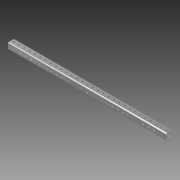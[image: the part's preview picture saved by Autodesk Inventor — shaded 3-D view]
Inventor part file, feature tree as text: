
AUTODESK INVENTOR PART (.ipt)
format: ipt  version: 2014 (Build 180170000, 170)  size: 184,320 bytes
history: native  units: in
note: dims shown in document units (in); Inventor stores cm internally (conversion verified against a paired STEP export)
features: sketch x3, extrude x2, chamfer x1, hole x1, pattern_linear x1
ambient origin geometry x8: Origin, YZ Plane, XZ Plane, XY Plane, X Axis, Y Axis, Z Axis, Center Point
bodies: Solid1 (feature_tree)
feature tree (8):
  extrude  "Extrusion1"  Depth=0.125in TaperAngle=45.0deg
  chamfer  "Chamfer1"  Distance=1.0in
  hole  "Hole1"  [1 undecoded]
  pattern_linear  "Rectangular Pattern1"  [2 undecoded]
  extrude  "Extrusion2"  [1 undecoded]
  sketch  "Sketch1"  dims[d0=30.0in d1=0.0in d2=0.125in d3=0.125in d4=45.0deg]
  sketch  "Sketch2"  dims[d5=0.5in]
  sketch  "Sketch3"  dims[d6=0.5in d7=0.264in d8=0.75in d9=0.375in d10=0.25in d11=0.5635in d12=1.0in d13=0.8108in d14=11.811in d16=1.0in d17=1.0in d18=0.0in]
note: 4 required parameter values undecoded (feature->parameter linkage not recoverable at this tier; creation-order binding heuristic only, values carry confidence <= 0.55)
